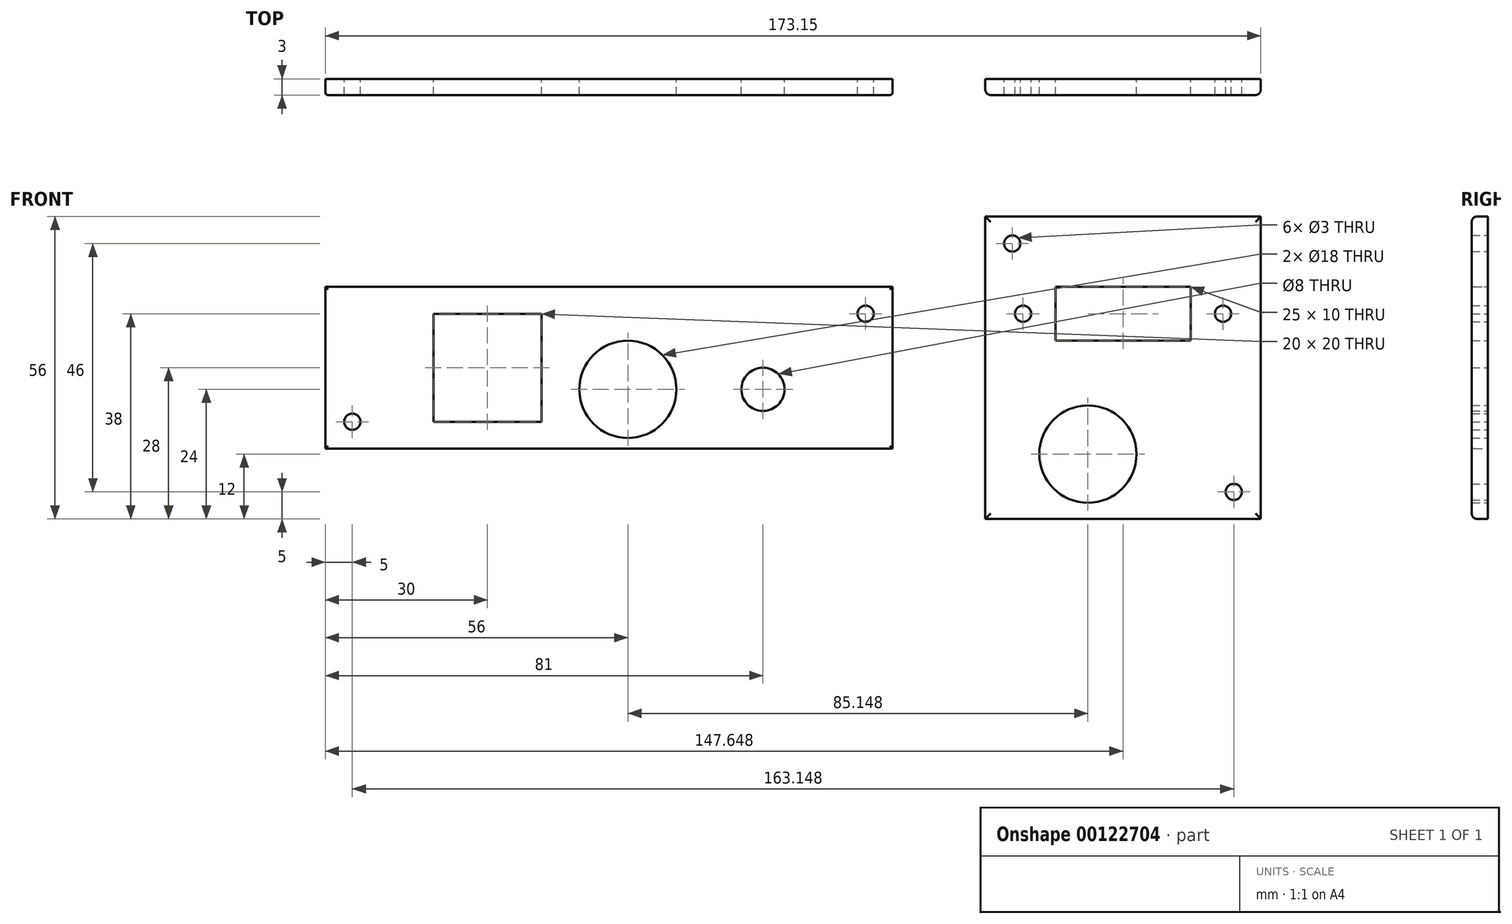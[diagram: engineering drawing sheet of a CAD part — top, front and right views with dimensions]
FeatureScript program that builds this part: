
annotation { "Feature Type Name" : "Feature", "Feature Type Description" : "" }
export const myFeature = defineFeature(function(context is Context, id is Id, definition is map)
    precondition{}
    {
        {
            var Q0;
            Q0=qCreatedBy(makeId("Front.planeOp"),FACE);
            var sketch = newSketch(context, id + "F0", { "sketchPlane" : qUnion([Q0])});
            skCircle(sketch, "E0", {"center": v(3.5, -4) * mm, "radius": 9 * mm});
            skLineSegment(sketch, "E1.bottom", {"start": v(-32.5, 10) * mm, "end": v(-12.5, 10) * mm});
            skLineSegment(sketch, "E1.top", {"start": v(-32.5, -10) * mm, "end": v(-12.5, -10) * mm});
            skLineSegment(sketch, "E1.left", {"start": v(-32.5, 10) * mm, "end": v(-32.5, -10) * mm});
            skLineSegment(sketch, "E1.right", {"start": v(-12.5, 10) * mm, "end": v(-12.5, -10) * mm});
            skCircle(sketch, "E2", {"center": v(28.5, -4) * mm, "radius": 4 * mm});
            skCircle(sketch, "E3", {"center": v(-47.5, -10) * mm, "radius": 1.5 * mm});
            skCircle(sketch, "E4", {"center": v(47.5, 10) * mm, "radius": 1.5 * mm});
            skLineSegment(sketch, "E5.bottom", {"start": v(52.5, -15) * mm, "end": v(-52.5, -15) * mm});
            skLineSegment(sketch, "E5.top", {"start": v(52.5, 15) * mm, "end": v(-52.5, 15) * mm});
            skLineSegment(sketch, "E5.left", {"start": v(52.5, -15) * mm, "end": v(52.5, 15) * mm});
            skLineSegment(sketch, "E5.right", {"start": v(-52.5, -15) * mm, "end": v(-52.5, 15) * mm});
            skPoint(sketch, "E5.middle", {"position": v(0, 0) * mm});
            skSolve(sketch);
        }
        {
            var Q0;
            Q0=makeQuery(id+"F0.imprint","IMPRINT",FACE,{"disambiguationData":[TD([[makeQuery(id+"F0.imprint","IMPRINT",EDGE,{"derivedFrom":sQuery(id+"F0.wireOp",EDGE,"E0")}),-1.0]])]});
            extrude(context, id + "F1", {"entities" : qUnion([Q0]), "depth" : 3 * mm});
        }
        {
            var Q0;
            Q0=makeQuery(id+"F1.opExtrude","CAP_EDGE",EDGE,{"disambiguationData":[OSD([sQuery(id+"F0.wireOp",EDGE,"E5.top")])],"isStart":false});
            var Q1;
            Q1=makeQuery(id+"F1.opExtrude","CAP_EDGE",EDGE,{"disambiguationData":[OSD([sQuery(id+"F0.wireOp",EDGE,"E5.right")])],"isStart":false});
            var Q2;
            Q2=makeQuery(id+"F1.opExtrude","CAP_EDGE",EDGE,{"disambiguationData":[OSD([sQuery(id+"F0.wireOp",EDGE,"E5.bottom")])],"isStart":false});
            var Q3;
            Q3=makeQuery(id+"F1.opExtrude","CAP_EDGE",EDGE,{"disambiguationData":[OSD([sQuery(id+"F0.wireOp",EDGE,"E5.left")])],"isStart":false});
            fillet(context, id + "F2", {"entities" : qUnion([Q0, Q1, Q2, Q3]), "radius" : 0.5 * mm, "tangentPropagation" : true, "allowEdgeOverflow" : false});
        }
        {
            var Q0;
            Q0=qCreatedBy(makeId("Front.planeOp"),FACE);
            var sketch = newSketch(context, id + "F3", { "sketchPlane" : qUnion([Q0])});
            skLineSegment(sketch, "E6.bottom", {"start": v(120.65, -28) * mm, "end": v(69.65, -28) * mm});
            skLineSegment(sketch, "E6.top", {"start": v(120.65, 28) * mm, "end": v(69.65, 28) * mm});
            skLineSegment(sketch, "E6.left", {"start": v(120.65, -28) * mm, "end": v(120.65, 28) * mm});
            skLineSegment(sketch, "E6.right", {"start": v(69.65, -28) * mm, "end": v(69.65, 28) * mm});
            skPoint(sketch, "E6.middle", {"position": v(95.15, 0) * mm});
            skCircle(sketch, "E7", {"center": v(74.65, 23) * mm, "radius": 1.5 * mm});
            skCircle(sketch, "E8", {"center": v(115.65, -23) * mm, "radius": 1.5 * mm});
            skCircle(sketch, "E9", {"center": v(88.65, -16) * mm, "radius": 9 * mm});
            skLineSegment(sketch, "E10.bottom", {"start": v(107.65, 5) * mm, "end": v(82.65, 5) * mm});
            skLineSegment(sketch, "E10.top", {"start": v(107.65, 15) * mm, "end": v(82.65, 15) * mm});
            skLineSegment(sketch, "E10.left", {"start": v(107.65, 5) * mm, "end": v(107.65, 15) * mm});
            skLineSegment(sketch, "E10.right", {"start": v(82.65, 5) * mm, "end": v(82.65, 15) * mm});
            skPoint(sketch, "E10.middle", {"position": v(95.15, 10) * mm});
            skCircle(sketch, "E11", {"center": v(76.65, 10) * mm, "radius": 1.5 * mm});
            skCircle(sketch, "E12", {"center": v(113.65, 10) * mm, "radius": 1.5 * mm});
            skSolve(sketch);
        }
        {
            var Q0;
            Q0=qSketchRegion(id+"F3",true);
            extrude(context, id + "F4", {"entities" : qUnion([Q0]), "depth" : 3 * mm});
        }
        {
            var Q0;
            Q0=makeQuery(id+"F4.opExtrude","CAP_EDGE",EDGE,{"disambiguationData":[OSD([sQuery(id+"F3.wireOp",EDGE,"E6.top")])],"isStart":false});
            var Q1;
            Q1=makeQuery(id+"F4.opExtrude","CAP_EDGE",EDGE,{"disambiguationData":[OSD([sQuery(id+"F3.wireOp",EDGE,"E6.right")])],"isStart":false});
            var Q2;
            Q2=makeQuery(id+"F4.opExtrude","CAP_EDGE",EDGE,{"disambiguationData":[OSD([sQuery(id+"F3.wireOp",EDGE,"E6.left")])],"isStart":false});
            var Q3;
            Q3=makeQuery(id+"F4.opExtrude","CAP_EDGE",EDGE,{"disambiguationData":[OSD([sQuery(id+"F3.wireOp",EDGE,"E6.bottom")])],"isStart":false});
            fillet(context, id + "F5", {"entities" : qUnion([Q0, Q1, Q2, Q3]), "radius" : 1 * mm, "tangentPropagation" : true, "allowEdgeOverflow" : false});
        }
    });
